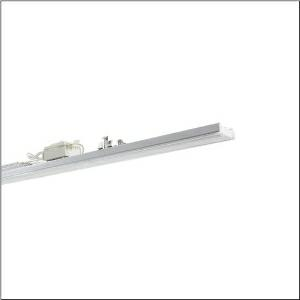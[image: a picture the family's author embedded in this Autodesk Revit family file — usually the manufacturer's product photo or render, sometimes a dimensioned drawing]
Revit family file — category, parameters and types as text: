
# Revit family: licross_11_recessed_ho_51tl12dnec5m
name_source: partatom
category: Lighting Fixtures
units: mm (PartAtom-declared; Revit-internal decimal feet)

## family parameters
Cut with Voids When Loaded = No
Host = Face
Light Source = No
Part Type = Normal
Room Calculation Point = No
Round Connector Dimension = Use Diameter
Shared = No

## types (1)
- --- (1 x LED, 12970 lm, 77 W, 5000K)
    Apparent Load = 77 VA
    CIE Flux Codes = 66 91 98 100 100
    Color Rendering = 90
    Color Temperature = 5000K
    Default Elevation = 1800 mm
    Description = Licross 11 Recessed HO, luminaire insert, of sheet steel, coil coated, white, length: 1.500mm, width: 66mm, height: 67mm, LED rated luminous flux: 12.970lm, light colour: 950, SDCM (Standard Deviation of Colour Matching)MacAdam ≤ 2 SDCM (initial), control gear: DALI 2, with plug, 5-pole, with phase selection, mains connection: 220..240V, AC, 50/60Hz, rated input power: 77W, internal wiring halogen-free, primary optical cover: cover, of PMMA, light emission: direct distribution, primary light characteristic: symmetric, protection rating (complete): IP40, insulation class (complete): insulation class I (protective earthing), certification: CE, ENEC, VDE, UKCA, protection symbol: D if used in an environment without relevant dust loads with corresponding accessories, impact resistance: IK06, permissible ambient temperature for indoor applications: -25..+30°C, corresponds to IFS (International Featured Standards) requirements for safety and quality in the food industry, reducing of maximum allowable ambient temperature of 5°C with ceiling mounting, LABS conformity tested according to VDMA 24364:2018-05, The light source and the operating device comply with the requirements of the Ecodesign Regulation (EU) 2019/2020 and are replaceable in accordance with this regulation, packaging unit: 1 piece
    Height = 58 mm
    Lamp = 1 x LED
    Lamp Light Flux = 12970 lm
    Lamp Power = 77 W
    Lamp count = 1
    Length = 1500 mm
    Luminous efficacy = 168 lm/W
    Manufacturer = Siteco
    ModVariant = No
    Model = 51TL12DNEC5M
    Mounting Place = Ceiling
    Mounting Type = Pendant
    Number of Poles = 1
    OnlyDefault = Yes
    Power Factor = 1
    Product Name = Licross 11 Recessed HO
    Product group = luminaire insert | ceiling pendant
    ProductGroupID = 901
    Protection Class = Protection class I
    Protection Degree = IP 40
    RLX_Detail_Level = 1
    RLX_Emergency_Light_Flux = 0 lm
    RLX_Emergency_Type = 0
    RLX_Emergency_Type_DB = No
    RlxData = <blob elided: 24765 chars, md5=1e5b0db8>
    Socket = socket
    Standby Power = 0 W
    System Light Flux = 12970 lm
    System Power = 77 W
    Type Comments = factory setting: luminous flux: 100 % | dim-lin: 254 | 522 mA
    Type Image = l_1296930.jpg
    URL = http://relux.com
    VarID = @adj_055973
    Voltage = 0 V
    Weight = 0.00 kg
    Width = 66 mm

## geometry (parser evidence)
native form markers: Blend x4, Sweep x10
no freeform markers — native parametric forms only
